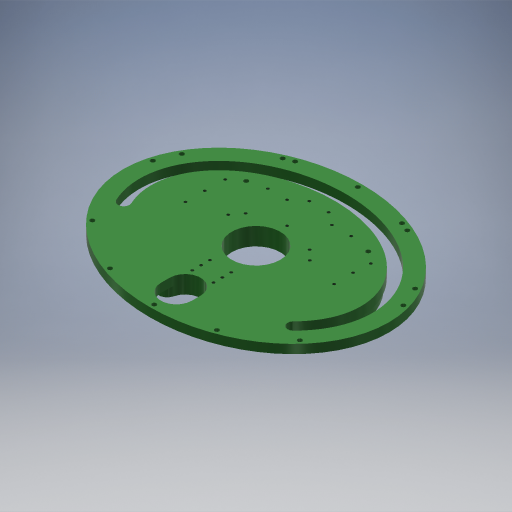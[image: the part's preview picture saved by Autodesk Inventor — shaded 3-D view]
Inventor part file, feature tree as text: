
AUTODESK INVENTOR PART (.ipt)
format: ipt  version: 2024.3 (Build 283343000, 343)  size: 530,432 bytes
history: native  units: mm
features: reference x19, sketch x12, projected_geometry x7, extrude x6, hole x6, other x3, fillet x1
ambient origin geometry x8: Origin, YZ Plane, XZ Plane, XY Plane, X Axis, Y Axis, Z Axis, Center Point
bodies: Volumenkörper1 (feature_tree)
feature tree (54):
  extrude  "Extrusion1"  Depth=240.0mm
  extrude  "Extrusion2"  Depth=10.0mm
  extrude  "Extrusion3"  Depth=31.5mm
  extrude  "Extrusion4"  TaperAngle=45.0deg  [1 undecoded]
  extrude  "Extrusion5"  Depth=12.894099mm
  hole  "Bohrung1"  [1 undecoded]
  hole  "Bohrung2"  [1 undecoded]
  hole  "Bohrung3"  [1 undecoded]
  hole  "Bohrung4"  [1 undecoded]
  hole  "Bohrung5"  [1 undecoded]
  hole  "Bohrung6"  [1 undecoded]
  extrude  "Extrusion6"  Depth=10.0mm
  fillet  "Rundung1"  Radius=145.0mm
  sketch  "Skizze15"  dims[d30=50.0mm d31=10.0mm d32=3.242mm d33=8.0mm d34=6.5mm d35=3.4mm d36=90.0deg d37=8.0mm d38=20.594885mm d39=5.2mm d40=10.0mm d41=4.0mm d42=2.0mm d43=90.0deg d44=14.2mm d45=20.594885mm d46=145.0mm d47=30.0deg d48=1.745329mm d49=5.2mm d50=10.0mm d51=4.0mm d52=2.0mm d53=90.0deg d54=8.0mm d55=20.594885mm d56=3.242mm d57=8.0mm d58=4.0mm d59=2.0mm d60=90.0deg d61=8.0mm d62=20.594885mm d63=60.0deg d64=60.0deg d65=95.0mm d66=95.0mm d67=3.242mm d68=8.0mm d69=4.0mm d70=2.0mm d71=90.0deg d72=8.0mm d73=20.594885mm d74=8.726646mm d75=8.726646mm d76=90.0mm d77=90.0mm d78=5.2mm d79=6.0mm d80=4.0mm d81=2.0mm d82=90.0deg d83=8.0mm d84=20.594885mm d85=10.0mm d86=0.0mm d87=0.0mm d88=10.0mm d89=10.0mm d90=25.714665mm d91=23.0mm]
  sketch  "Skizze2"  dims[d0=300.0mm d1=240.0mm]
  projected_geometry  "Projizierte Kontur1"
  sketch  "Skizze3"  dims[d2=10.0mm d3=0.0mm d7=18.5mm]
  projected_geometry  "Projizierte Kontur2"
  reference  "Referenz1"
  sketch  "Skizze4"  dims[d8=18.5mm d9=31.5mm]
  sketch  "Skizze5"  dims[d10=31.5mm d11=45.0deg]
  sketch  "Skizze6"  dims[d12=90.0deg d13=12.894099mm]
  sketch  "Skizze7"  dims[d14=30.0deg d15=15.0deg]
  reference  "Referenz2"
  sketch  "Skizze9"  dims[d16=0.0mm d17=0.0mm d18=34.0mm]
  projected_geometry  "Projizierte Kontur4"
  sketch  "Skizze10"  dims[d19=34.0mm d20=10.0mm d21=0.0mm]
  reference  "Referenz3"
  reference  "Referenz4"
  reference  "Referenz5"
  reference  "Referenz6"
  reference  "Referenz7"
  reference  "Referenz8"
  reference  "Referenz9"
  reference  "Referenz10"
  reference  "Referenz11"
  reference  "Referenz12"
  reference  "Referenz13"
  projected_geometry  "Projizierte Kontur5"
  reference  "Referenz14"
  reference  "Referenz15"
  reference  "Referenz16"
  reference  "Referenz17"
  sketch  "Skizze11"  dims[d22=35.0mm d23=80.0mm]
  projected_geometry  "Projizierte Kontur6"
  sketch  "Skizze13"  dims[d24=10.0mm d25=0.0mm d26=55.0mm]
  projected_geometry  "Projizierte Kontur7"
  sketch  "Skizze14"  dims[d27=0.0mm d28=0.0mm d29=24.0mm]
  projected_geometry  "Projizierte Kontur8"
  reference  "Referenz18"
  reference  "Referenz19"
  other  "<path> - Kompass, Gehäuse\24_0497_0001.iam"
  other  "24_0497_0001.iam"
  other  "Alle_Schalter:1"
note: 7 required parameter values undecoded (feature->parameter linkage not recoverable at this tier; creation-order binding heuristic only, values carry confidence <= 0.55)
note: 1 file-system path scrubbed to <path> (originals preserved in map.json)
